# Revit family: QF_BOURGEAT_2_silos_fixe
name_source: partatom
category: Equipement spécialisé
revit_build: Autodesk Revit 2015 (Build: 20140606_1530(x64)
units: mm (PartAtom-declared; Revit-internal decimal feet)

## types (3) — shared parameters
Fabricant = BOURGEAT
Hauteur hors tout = 900 mm  [stored 2.95276 ft]
Spécification du Fabricant = SILOS FIXE
URL catalogue = http://www.bourgeat.fr

## per-type parameters (varying)
| type | Charge max | Frequence | Indice de protection | Intensité nominale | Longueur hors tout | Modèle | Phase | Poids net à vide | Profondeur hors tout | Puissance électrique  | Tension |
| chauffant_non_ventile_assiettes_200/260 | 140.00 kg | 50/60Hz | 25 | 4 A | 442 mm  [stored 1.45013 ft] | 777326+777435 | 2 | 37.00 kg | 898 mm  [stored 2.94619 ft] | 950 W | 230 V |
| chauffant_non_ventile_assiettes_260/320 | 160.00 kg | 50/60Hz | 25 | 6 A | 510 mm  [stored 1.67323 ft] | 777332+777440 | 2 | 40.00 kg | 990 mm  [stored 3.24803 ft] | 1400 W | 230 V |
| neutre_assiettes200/260 | 160.00 kg | 0 |  | 0 A | 510 mm  [stored 1.67323 ft] | 777301+777435 | 0 | 50.00 kg | 990 mm  [stored 3.24803 ft] | 0 W | 0 V |

note: [stored X ft] marks values corroborated as IEEE doubles in the binary element streams (Revit-internal decimal feet)
